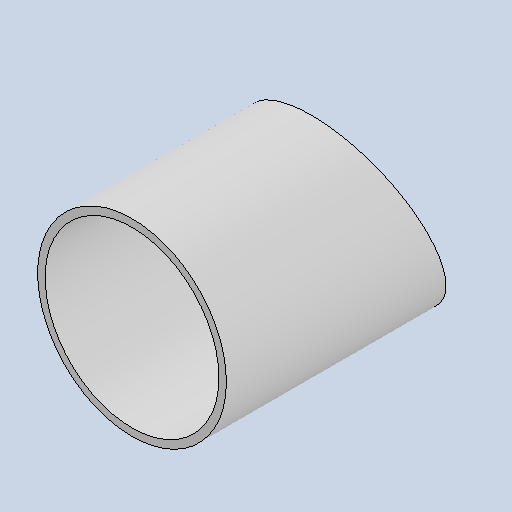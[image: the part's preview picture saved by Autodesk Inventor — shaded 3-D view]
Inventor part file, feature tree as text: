
AUTODESK INVENTOR PART (.ipt)
format: ipt  version: 2025 (Build 290162010, 162A)  size: 115,712 bytes
history: native  units: mm
features: extrude x2, sketch x2, projected_geometry x1
ambient origin geometry x8: Origin, YZ Plane, XZ Plane, XY Plane, X Axis, Y Axis, Z Axis, Center Point
bodies: Solid1 (feature_tree)
feature tree (5):
  extrude  "Extrusion1"  Depth=3.0mm
  extrude  "Extrusion2"  Depth=100.0mm
  sketch  "Sketch1"  dims[d0=76.1mm d1=3.0mm]
  sketch  "Sketch2"  dims[d2=100.0mm d3=0.0mm d4=3.490659mm d5=60.0mm d6=0.0mm]
  projected_geometry  "Projected Loop1"
